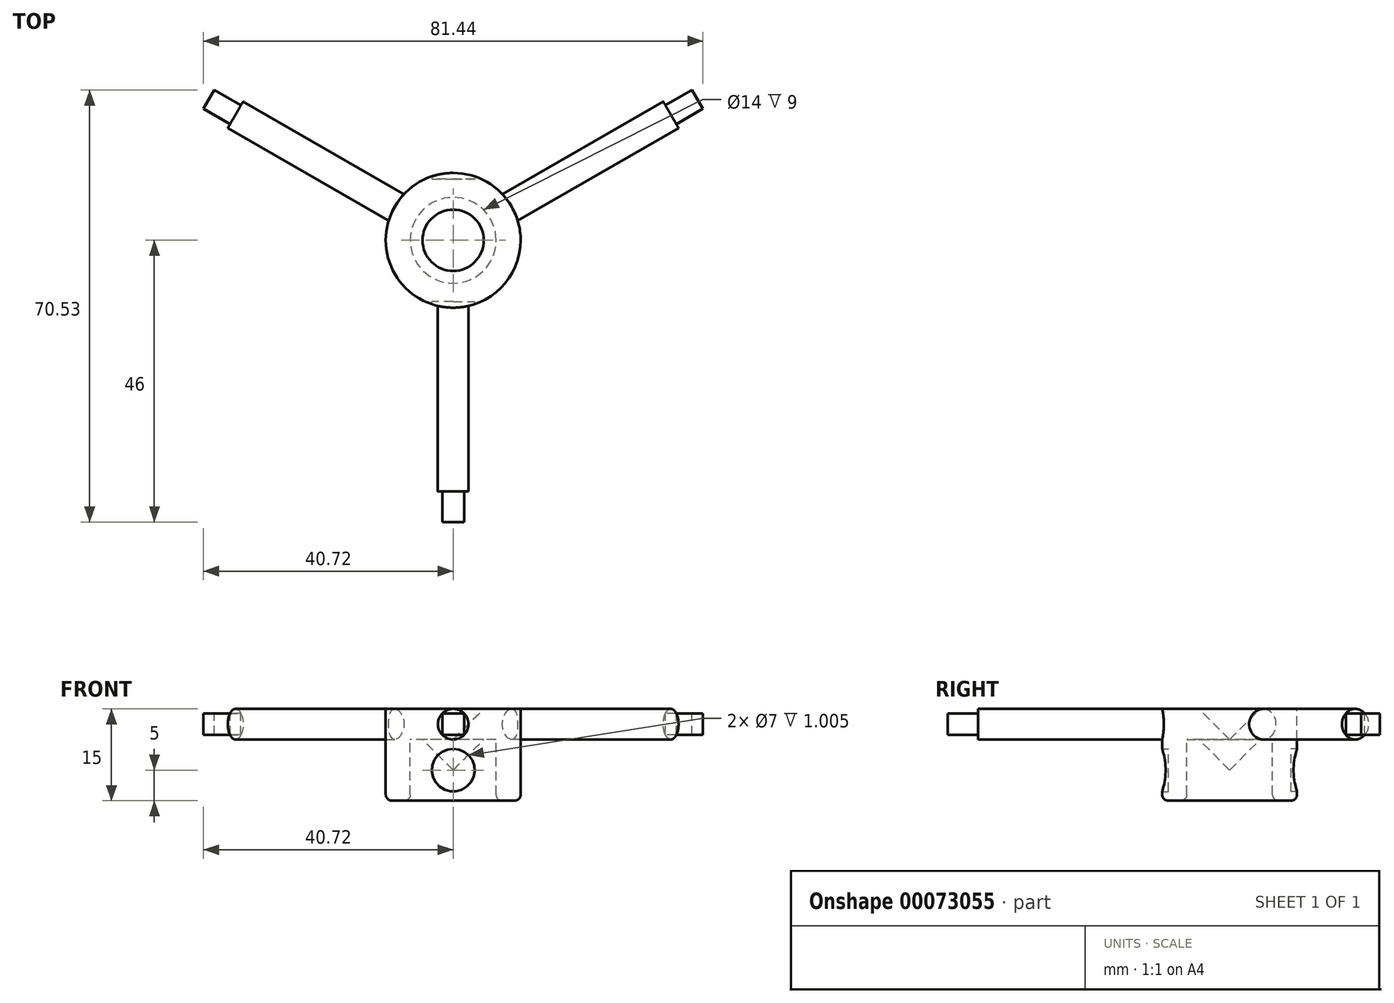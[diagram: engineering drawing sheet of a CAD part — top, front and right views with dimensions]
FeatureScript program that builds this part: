
annotation { "Feature Type Name" : "Feature", "Feature Type Description" : "" }
export const myFeature = defineFeature(function(context is Context, id is Id, definition is map)
    precondition{}
    {
        {
            var Q0;
            Q0=qCreatedBy(makeId("Front.planeOp"),FACE);
            var sketch = newSketch(context, id + "F10", { "sketchPlane" : qUnion([Q0])});
            skLineSegment(sketch, "E0", {"start": v(0, -10) * mm, "end": v(5, -5) * mm});
            skLineSegment(sketch, "E1", {"start": v(5, -5) * mm, "end": v(7, -5) * mm});
            skLineSegment(sketch, "E2", {"start": v(7, -5) * mm, "end": v(7, -15) * mm});
            skLineSegment(sketch, "E3", {"start": v(7, -15) * mm, "end": v(11, -15) * mm});
            skLineSegment(sketch, "E4", {"start": v(11, -15) * mm, "end": v(11, 0) * mm});
            skLineSegment(sketch, "E5", {"start": v(11, 0) * mm, "end": v(5, 0) * mm});
            skLineSegment(sketch, "E6", {"start": v(5, 0) * mm, "end": v(0, -5) * mm});
            skLineSegment(sketch, "E7", {"start": v(0, 74.7) * mm, "end": v(0, -74.96) * mm, "construction": true});
            skLineSegment(sketch, "E8", {"start": v(0, -5) * mm, "end": v(0, -10) * mm});
            skSolve(sketch);
        }
        {
            var Q0;
            Q0=makeQuery(id+"F10.imprint","IMPRINT",FACE,{"disambiguationData":[TD([[makeQuery(id+"F10.imprint","IMPRINT",EDGE,{"derivedFrom":sQuery(id+"F10.wireOp",EDGE,"E0")}),1.0]])]});
            var Q1;
            Q1=sQuery(id+"F10.wireOp",EDGE,"E6");
            var Q2;
            Q2=sQuery(id+"F10.wireOp",EDGE,"E5");
            var Q3;
            Q3=sQuery(id+"F10.wireOp",EDGE,"E4");
            var Q4;
            Q4=sQuery(id+"F10.wireOp",EDGE,"E3");
            var Q5;
            Q5=sQuery(id+"F10.wireOp",EDGE,"E2");
            var Q6;
            Q6=sQuery(id+"F10.wireOp",EDGE,"E1");
            var Q7;
            Q7=sQuery(id+"F10.wireOp",EDGE,"E0");
            var Q8;
            Q8=sQuery(id+"F10.wireOp",EDGE,"E7");
            revolve(context, id + "F11", {"entities" : qUnion([Q0]), "surfaceEntities" : qUnion([Q1, Q2, Q3, Q4, Q5, Q6, Q7]), "axis" : qUnion([Q8]), "revolveType" : RevolveType.FULL});
        }
        {
            var Q0;
            Q0=qCreatedBy(makeId("Front.planeOp"),FACE);
            cPlane(context, id + "F0", {"entities" : qUnion([Q0]), "cplaneType" : CPlaneType.OFFSET, "offset" : 11 * mm, "width" : 152.4 * mm, "height" : 152.4 * mm});
        }
        {
            var Q0;
            Q0=qCreatedBy(id+"F0.planeOp",FACE);
            var sketch = newSketch(context, id + "F1", { "sketchPlane" : qUnion([Q0])});
            skCircle(sketch, "E9", {"center": v(0, -2.5) * mm, "radius": 2.5 * mm});
            skSolve(sketch);
        }
        {
            var Q0;
            Q0 = qSketchRegion(id + "F1", true);
            extrude(context, id + "F2", {"entities" : qUnion([Q0]), "operationType" : NewBodyOperationType.ADD, "depth" : 30 * mm, "hasSecondDirection" : true, "secondDirectionOppositeDirection" : true, "secondDirectionDepth" : 2 * mm});
        }
        {
            var Q0;
            Q0=makeQuery(id+"F2.opExtrude","CAP_FACE",FACE,{"disambiguationData":[OSD([sQuery(id+"F1.wireOp",EDGE,"E9")])],"isStart":false});
            var sketch = newSketch(context, id + "F3", { "sketchPlane" : qUnion([Q0])});
            skLineSegment(sketch, "E10.bottom", {"start": v(-1.77, -4.27) * mm, "end": v(1.77, -4.27) * mm});
            skLineSegment(sketch, "E10.top", {"start": v(-1.77, -0.73) * mm, "end": v(1.77, -0.73) * mm});
            skLineSegment(sketch, "E10.left", {"start": v(-1.77, -4.27) * mm, "end": v(-1.77, -0.73) * mm});
            skLineSegment(sketch, "E10.right", {"start": v(1.77, -4.27) * mm, "end": v(1.77, -0.73) * mm});
            skSolve(sketch);
        }
        {
            var Q0;
            Q0 = qSketchRegion(id + "F3", true);
            extrude(context, id + "F4", {"entities" : qUnion([Q0]), "operationType" : NewBodyOperationType.ADD, "depth" : 5 * mm});
        }
        {
            var Q0;
            Q0=makeQuery(id+"F2.opExtrude","SWEPT_BODY",BODY,{"disambiguationData":[OSD([sQuery(id+"F1.wireOp",EDGE,"E9")])]});
            var Q1;
            Q1=makeQuery(id+"F11.opRevolve","SWEPT_BODY",BODY,{"disambiguationData":[OSD([sQuery(id+"F10.wireOp",EDGE,"E0"),sQuery(id+"F10.wireOp",EDGE,"E1"),sQuery(id+"F10.wireOp",EDGE,"E2"),sQuery(id+"F10.wireOp",EDGE,"E3"),sQuery(id+"F10.wireOp",EDGE,"E4"),sQuery(id+"F10.wireOp",EDGE,"E5"),sQuery(id+"F10.wireOp",EDGE,"E6"),sQuery(id+"F10.wireOp",EDGE,"E8")])]});
            var Q2;
            Q2=makeQuery(id+"F11.opRevolve","SWEPT_FACE",FACE,{"disambiguationData":[OSD([sQuery(id+"F10.wireOp",EDGE,"E4")])]});
            circularPattern(context, id + "F5", {"operationType" : NewBodyOperationType.ADD, "entities" : qUnion([Q0, Q1]), "axis" : qUnion([Q2]), "angle" : 360 * degree, "instanceCount" : 3, "equalSpace" : true});
        }
        {
            var Q0;
            Q0=makeQuery(id+"F11.opRevolve","SWEPT_EDGE",EDGE,{"disambiguationData":[OSD([sQuery(id+"F10.wireOp",VERTEX,"E3.end")])]});
            var Q1;
            Q1=makeQuery(id+"F11.opRevolve","SWEPT_EDGE",EDGE,{"disambiguationData":[OSD([sQuery(id+"F10.wireOp",VERTEX,"E2.end")])]});
            var Q2;
            Q2=makeQuery(id+"F11.opRevolve","SWEPT_EDGE",EDGE,{"disambiguationData":[OSD([sQuery(id+"F10.wireOp",EDGE,"E3"),sQuery(id+"F10.wireOp",EDGE,"E4")])]});
            var Q3;
            Q3=makeQuery(id+"F11.opRevolve","SWEPT_EDGE",EDGE,{"disambiguationData":[OSD([sQuery(id+"F10.wireOp",EDGE,"E2"),sQuery(id+"F10.wireOp",EDGE,"E3")])]});
            fillet(context, id + "F6", {"entities" : qUnion([Q0, Q1, Q2, Q3]), "radius" : 1 * mm, "tangentPropagation" : true, "allowEdgeOverflow" : false});
        }
        {
            var Q0;
            Q0=qCreatedBy(makeId("Front.planeOp"),FACE);
            var sketch = newSketch(context, id + "F7", { "sketchPlane" : qUnion([Q0])});
            skCircle(sketch, "E11", {"center": v(0, -10) * mm, "radius": 3.5 * mm});
            skSolve(sketch);
        }
        {
            var Q0;
            Q0=makeQuery(id+"F7.imprint","IMPRINT",FACE,{"disambiguationData":[TD([[makeQuery(id+"F7.imprint","IMPRINT",EDGE,{"derivedFrom":sQuery(id+"F7.wireOp",EDGE,"E11")}),1.0]])]});
            extrude(context, id + "F8", {"entities" : qUnion([Q0]), "operationType" : NewBodyOperationType.REMOVE, "depth" : 12 * mm, "hasSecondDirection" : true, "secondDirectionOppositeDirection" : false, "secondDirectionDepth" : 10 * mm});
        }
        {
            var Q0;
            Q0 = qSketchRegion(id + "F7", true);
            extrude(context, id + "F9", {"entities" : qUnion([Q0]), "operationType" : NewBodyOperationType.REMOVE, "oppositeDirection" : true, "depth" : 12 * mm, "hasSecondDirection" : true, "secondDirectionOppositeDirection" : true, "secondDirectionDepth" : 10 * mm});
        }
    });
